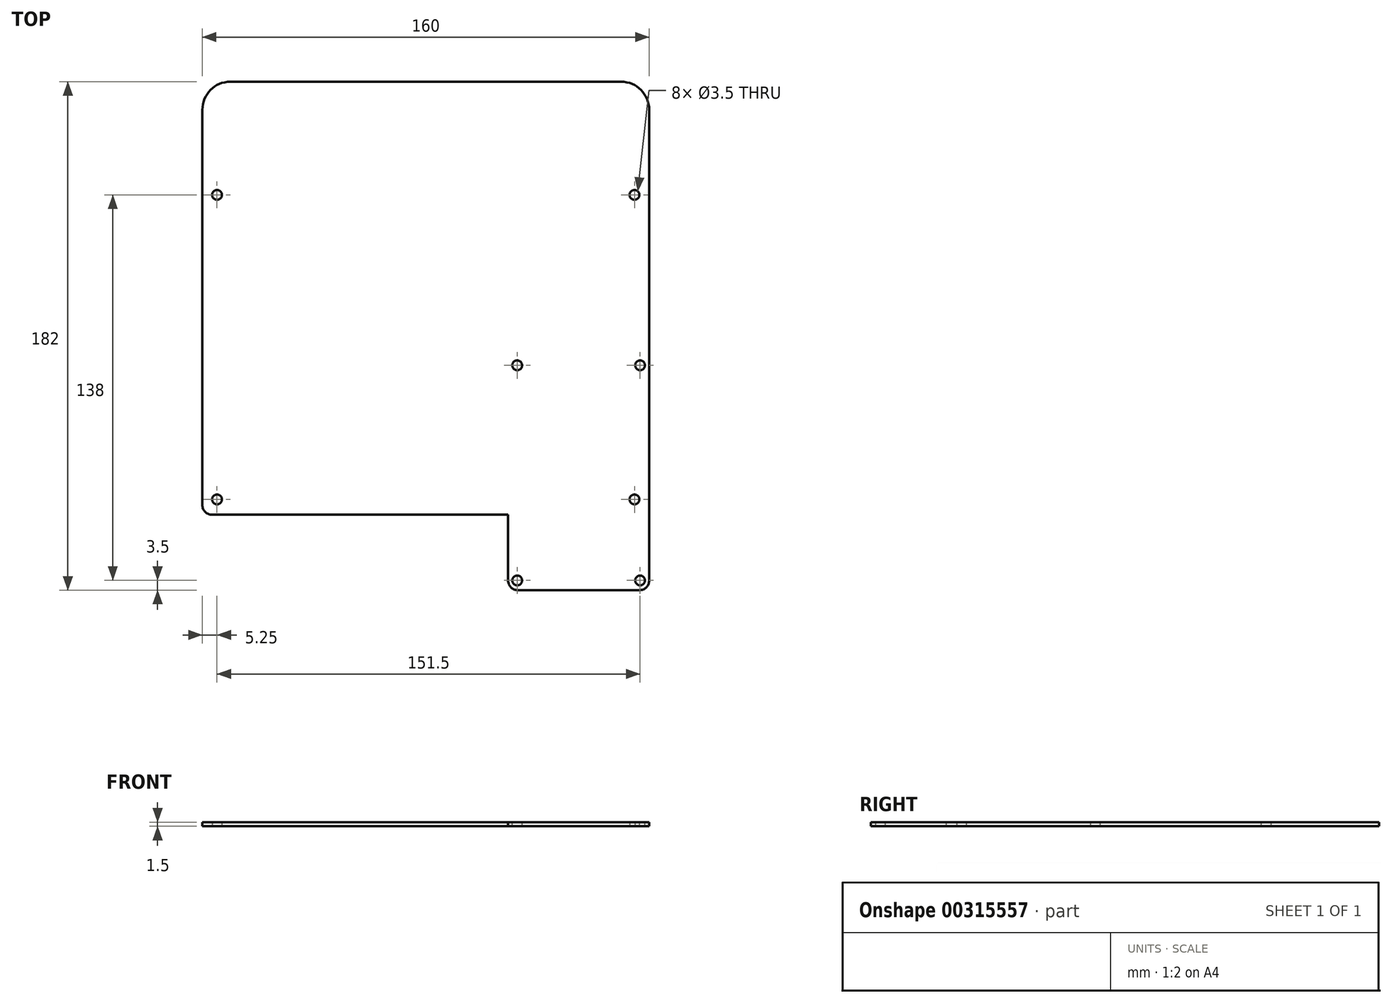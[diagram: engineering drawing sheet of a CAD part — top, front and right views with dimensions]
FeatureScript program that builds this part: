
annotation { "Feature Type Name" : "Feature", "Feature Type Description" : "" }
export const myFeature = defineFeature(function(context is Context, id is Id, definition is map)
    precondition{}
    {
        {
            var Q0;
            Q0=qCreatedBy(makeId("Top.planeOp"),FACE);
            var sketch = newSketch(context, id + "F0", { "sketchPlane" : qUnion([Q0])});
            skCircle(sketch, "E0", {"center": v(-74.75, 37) * mm, "radius": 1.75 * mm});
            skCircle(sketch, "E1", {"center": v(74.75, 37) * mm, "radius": 1.75 * mm});
            skCircle(sketch, "E2", {"center": v(-74.75, -72) * mm, "radius": 1.75 * mm});
            skCircle(sketch, "E3", {"center": v(74.75, -72) * mm, "radius": 1.75 * mm});
            skLineSegment(sketch, "E4.bottom", {"start": v(74.75, 37) * mm, "end": v(-74.75, 37) * mm, "construction": true});
            skLineSegment(sketch, "E4.top", {"start": v(74.75, -72) * mm, "end": v(-74.75, -72) * mm, "construction": true});
            skLineSegment(sketch, "E4.left", {"start": v(74.75, 37) * mm, "end": v(74.75, -72) * mm, "construction": true});
            skLineSegment(sketch, "E4.right", {"start": v(-74.75, 37) * mm, "end": v(-74.75, -72) * mm, "construction": true});
            skPoint(sketch, "E4.middle", {"position": v(0, 0) * mm});
            skLineSegment(sketch, "E5.bottom", {"start": v(80, 77.5) * mm, "end": v(-80, 77.5) * mm});
            skLineSegment(sketch, "E5.top", {"start": v(80, -77.5) * mm, "end": v(-80, -77.5) * mm});
            skLineSegment(sketch, "E5.left", {"start": v(80, 77.5) * mm, "end": v(80, -77.5) * mm});
            skLineSegment(sketch, "E5.right", {"start": v(-80, 77.5) * mm, "end": v(-80, -77.5) * mm});
            skSolve(sketch);
        }
        {
            var Q0;
            Q0 = qSketchRegion(id + "F0", true);
            extrude(context, id + "F1", {"entities" : qUnion([Q0]), "depth" : 1.5 * mm});
        }
        {
            var Q0;
            Q0=qCreatedBy(makeId("Top.planeOp"),FACE);
            var sketch = newSketch(context, id + "F2", { "sketchPlane" : qUnion([Q0])});
            skLineSegment(sketch, "E6.bottom", {"start": v(80, -104.5) * mm, "end": v(29.5, -104.5) * mm});
            skLineSegment(sketch, "E6.top", {"start": v(80, -77.5) * mm, "end": v(29.5, -77.5) * mm});
            skLineSegment(sketch, "E6.left", {"start": v(80, -104.5) * mm, "end": v(80, -77.5) * mm});
            skLineSegment(sketch, "E6.right", {"start": v(29.5, -104.5) * mm, "end": v(29.5, -77.5) * mm});
            skSolve(sketch);
        }
        {
            var Q0;
            Q0 = qSketchRegion(id + "F2", true);
            extrude(context, id + "F3", {"entities" : qUnion([Q0]), "operationType" : NewBodyOperationType.ADD, "depth" : 1.5 * mm});
        }
        {
            var Q0;
            Q0=makeQuery(id+"F3.boolean.opBoolean","MERGE",FACE,{"derivedFrom":[makeQuery(id+"F1.opExtrude","CAP_FACE",FACE,{"disambiguationData":[OSD([sQuery(id+"F0.wireOp",EDGE,"E0"),sQuery(id+"F0.wireOp",EDGE,"E1"),sQuery(id+"F0.wireOp",EDGE,"E2"),sQuery(id+"F0.wireOp",EDGE,"E3"),sQuery(id+"F0.wireOp",EDGE,"E5.bottom"),sQuery(id+"F0.wireOp",EDGE,"E5.top"),sQuery(id+"F0.wireOp",EDGE,"E5.left"),sQuery(id+"F0.wireOp",EDGE,"E5.right")])],"isStart":false}),makeQuery(id+"F3.opExtrude","CAP_FACE",FACE,{"disambiguationData":[OSD([sQuery(id+"F2.wireOp",EDGE,"E6.bottom"),sQuery(id+"F2.wireOp",EDGE,"E6.top"),sQuery(id+"F2.wireOp",EDGE,"E6.left"),sQuery(id+"F2.wireOp",EDGE,"E6.right")])],"isStart":false})]});
            var sketch = newSketch(context, id + "F4", { "sketchPlane" : qUnion([Q0])});
            skLineSegment(sketch, "E7.bottom", {"start": v(76.75, -101) * mm, "end": v(32.75, -101) * mm, "construction": true});
            skLineSegment(sketch, "E7.top", {"start": v(76.75, -24) * mm, "end": v(32.75, -24) * mm, "construction": true});
            skLineSegment(sketch, "E7.left", {"start": v(76.75, -101) * mm, "end": v(76.75, -24) * mm, "construction": true});
            skLineSegment(sketch, "E7.right", {"start": v(32.75, -101) * mm, "end": v(32.75, -24) * mm, "construction": true});
            skLineSegment(sketch, "E8", {"start": v(54.75, -104.5) * mm, "end": v(54.75, -20.7) * mm, "construction": true});
            skCircle(sketch, "E9", {"center": v(76.75, -101) * mm, "radius": 1.75 * mm});
            skCircle(sketch, "E10", {"center": v(32.75, -101) * mm, "radius": 1.75 * mm});
            skCircle(sketch, "E11", {"center": v(32.75, -24) * mm, "radius": 1.75 * mm});
            skCircle(sketch, "E12", {"center": v(76.75, -24) * mm, "radius": 1.75 * mm});
            skSolve(sketch);
        }
        {
            var Q0;
            Q0 = qSketchRegion(id + "F4", true);
            extrude(context, id + "F5", {"entities" : qUnion([Q0]), "operationType" : NewBodyOperationType.REMOVE, "oppositeDirection" : true, "depth" : 25 * mm});
        }
        {
            var Q0;
            Q0=makeQuery(id+"F3.opExtrude","SWEPT_EDGE",EDGE,{"disambiguationData":[OSD([sQuery(id+"F2.wireOp",EDGE,"E6.bottom"),sQuery(id+"F2.wireOp",EDGE,"E6.left")])]});
            var Q1;
            Q1=makeQuery(id+"F3.opExtrude","SWEPT_EDGE",EDGE,{"disambiguationData":[OSD([sQuery(id+"F2.wireOp",EDGE,"E6.bottom"),sQuery(id+"F2.wireOp",EDGE,"E6.right")])]});
            var Q2;
            Q2=makeQuery(id+"F3.opExtrude","SWEPT_EDGE",EDGE,{"disambiguationData":[OSD([sQuery(id+"F2.wireOp",EDGE,"E6.top"),sQuery(id+"F2.wireOp",EDGE,"E6.right")])]});
            var Q3;
            Q3=makeQuery(id+"F1.opExtrude","SWEPT_EDGE",EDGE,{"disambiguationData":[OSD([sQuery(id+"F0.wireOp",EDGE,"E5.top"),sQuery(id+"F0.wireOp",EDGE,"E5.right")])]});
            fillet(context, id + "F6", {"entities" : qUnion([Q0, Q1, Q2, Q3]), "radius" : 3.5 * mm, "tangentPropagation" : true, "allowEdgeOverflow" : false});
        }
        {
            var Q0;
            Q0=makeQuery(id+"F1.opExtrude","SWEPT_EDGE",EDGE,{"disambiguationData":[OSD([sQuery(id+"F0.wireOp",EDGE,"E5.bottom"),sQuery(id+"F0.wireOp",EDGE,"E5.left")])]});
            var Q1;
            Q1=makeQuery(id+"F1.opExtrude","SWEPT_EDGE",EDGE,{"disambiguationData":[OSD([sQuery(id+"F0.wireOp",EDGE,"E5.bottom"),sQuery(id+"F0.wireOp",EDGE,"E5.right")])]});
            fillet(context, id + "F7", {"entities" : qUnion([Q0, Q1]), "radius" : 10 * mm, "tangentPropagation" : true, "allowEdgeOverflow" : false});
        }
    });
